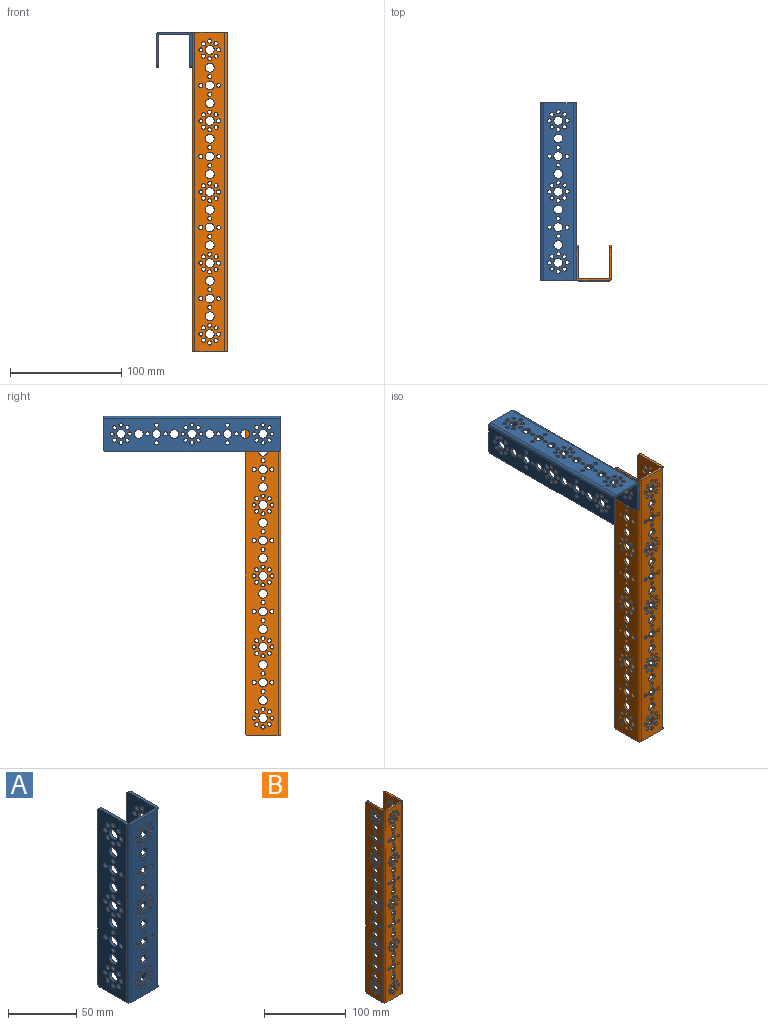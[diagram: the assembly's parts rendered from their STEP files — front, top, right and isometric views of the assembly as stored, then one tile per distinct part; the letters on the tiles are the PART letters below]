
ASSEMBLY  parts=2 mates=1
PART A: 141 faces, bbox 32x32x160 mm
  f0: cylinder r=2.5mm len=160mm, axis (0,0,-1), area 628.3mm2, adj f1,f11,f12,f13
  f1: plane 160x27mm, normal (0,-1,0), area 3523.5mm2, adj f0,f2,f12,f13,f18,f23,f24,f25
  f2: cylinder r=2.5mm len=160mm, axis (0,0,-1), area 628.3mm2, adj f1,f3,f12,f13
  f3: plane 160x29.5mm, normal (1,0,0), area 3920.9mm2, adj f2,f4,f12,f13,f14,f17,f20,f22
  f4: plane 155x2mm, normal (0,1,0), area 310mm2, adj f3,f5,f14,f17
  f5: plane 160x29.5mm, normal (-1,0,0), area 3920.9mm2, adj f4,f6,f12,f13,f14,f17,f20,f22
  f6: cylinder r=0.5mm len=160mm, axis (0,0,-1), area 125.7mm2, adj f5,f7,f12,f13
  f7: plane 160x27mm, normal (0,1,0), area 3523.5mm2, adj f6,f8,f12,f13,f18,f23,f24,f25
  f8: cylinder r=0.5mm len=160mm, axis (0,0,-1), area 125.7mm2, adj f7,f9,f12,f13
  f9: plane 160x29.5mm, normal (1,0,0), area 3920.9mm2, adj f8,f10,f12,f13,f15,f16,f19,f21
  f10: plane 155x2mm, normal (0,1,0), area 310mm2, adj f9,f11,f15,f16
  f11: plane 160x29.5mm, normal (-1,0,0), area 3920.9mm2, adj f0,f10,f12,f13,f15,f16,f19,f21
  f12: plane 32x29.5mm, normal (0,0,1), area 171.4mm2, adj f0,f1,f2,f3,f5,f6,f7,f8
  f13: plane 32x29.5mm, normal (0,0,-1), area 171.4mm2, adj f0,f1,f2,f3,f5,f6,f7,f8
  f14: cylinder r=2.5mm len=2.5mm, axis (1,0,0), area 7.9mm2, adj f3,f4,f5,f12
  f15: cylinder r=2.5mm len=2.5mm, axis (1,0,0), area 7.9mm2, adj f9,f10,f11,f12
  f16: cylinder r=2.5mm len=2.5mm, axis (-1,0,0), area 7.9mm2, adj f9,f10,f11,f13
  f17: cylinder r=2.5mm len=2.5mm, axis (-1,0,0), area 7.9mm2, adj f3,f4,f5,f13
  f18: cylinder r=4mm len=8mm, axis (0,-1,0), area 50.3mm2, adj f1,f7
  f19: cylinder r=4mm len=8mm, axis (-1,0,0), area 50.3mm2, adj f9,f11
  f20: cylinder r=4mm len=8mm, axis (-1,0,0), area 50.3mm2, adj f3,f5
  f21: cylinder r=1.85mm len=3.7mm, axis (-1,0,0), area 23.2mm2, adj f9,f11
  f22: cylinder r=1.85mm len=3.7mm, axis (-1,0,0), area 23.2mm2, adj f3,f5
  f23: cylinder r=1.85mm len=3.7mm, axis (0,-1,0), area 23.2mm2, adj f1,f7
  f24: cylinder r=4mm len=8mm, axis (0,-1,0), area 50.3mm2, adj f1,f7
  f25: cylinder r=4mm len=8mm, axis (0,-1,0), area 50.3mm2, adj f1,f7
  f26: cylinder r=4mm len=8mm, axis (0,-1,0), area 50.3mm2, adj f1,f7
  f27: cylinder r=4mm len=8mm, axis (0,-1,0), area 50.3mm2, adj f1,f7
  f28: cylinder r=4mm len=8mm, axis (0,-1,0), area 50.3mm2, adj f1,f7
  f29: cylinder r=4mm len=8mm, axis (0,-1,0), area 50.3mm2, adj f1,f7
  f30: cylinder r=4mm len=8mm, axis (0,-1,0), area 50.3mm2, adj f1,f7
  f31: cylinder r=4mm len=8mm, axis (0,-1,0), area 50.3mm2, adj f1,f7
  f32: cylinder r=4mm len=8mm, axis (-1,0,0), area 50.3mm2, adj f9,f11
  f33: cylinder r=4mm len=8mm, axis (-1,0,0), area 50.3mm2, adj f3,f5
  f34: cylinder r=4mm len=8mm, axis (-1,0,0), area 50.3mm2, adj f9,f11
  f35: cylinder r=4mm len=8mm, axis (-1,0,0), area 50.3mm2, adj f3,f5
  f36: cylinder r=4mm len=8mm, axis (-1,0,0), area 50.3mm2, adj f9,f11
  f37: cylinder r=4mm len=8mm, axis (-1,0,0), area 50.3mm2, adj f3,f5
  f38: cylinder r=4mm len=8mm, axis (-1,0,0), area 50.3mm2, adj f9,f11
  f39: cylinder r=4mm len=8mm, axis (-1,0,0), area 50.3mm2, adj f3,f5
  f40: cylinder r=4mm len=8mm, axis (-1,0,0), area 50.3mm2, adj f9,f11
  f41: cylinder r=4mm len=8mm, axis (-1,0,0), area 50.3mm2, adj f3,f5
  f42: cylinder r=4mm len=8mm, axis (-1,0,0), area 50.3mm2, adj f9,f11
  f43: cylinder r=4mm len=8mm, axis (-1,0,0), area 50.3mm2, adj f3,f5
  f44: cylinder r=4mm len=8mm, axis (-1,0,0), area 50.3mm2, adj f9,f11
  f45: cylinder r=4mm len=8mm, axis (-1,0,0), area 50.3mm2, adj f3,f5
  f46: cylinder r=4mm len=8mm, axis (-1,0,0), area 50.3mm2, adj f9,f11
  f47: cylinder r=4mm len=8mm, axis (-1,0,0), area 50.3mm2, adj f3,f5
  f48: cylinder r=1.85mm len=3.7mm, axis (0,-1,0), area 23.2mm2, adj f1,f7
  f49: cylinder r=1.85mm len=3.7mm, axis (0,-1,0), area 23.2mm2, adj f1,f7
  f50: cylinder r=1.85mm len=3.7mm, axis (0,-1,0), area 23.2mm2, adj f1,f7
  f51: cylinder r=1.85mm len=3.7mm, axis (0,-1,0), area 23.2mm2, adj f1,f7
  f52: cylinder r=1.85mm len=3.7mm, axis (0,-1,0), area 23.2mm2, adj f1,f7
  f53: cylinder r=1.85mm len=3.7mm, axis (0,-1,0), area 23.2mm2, adj f1,f7
  f54: cylinder r=1.85mm len=3.7mm, axis (0,-1,0), area 23.2mm2, adj f1,f7
  f55: cylinder r=1.85mm len=3.7mm, axis (-1,0,0), area 23.2mm2, adj f9,f11
  f56: cylinder r=1.85mm len=3.7mm, axis (-1,0,0), area 23.2mm2, adj f3,f5
  f57: cylinder r=1.85mm len=3.7mm, axis (-1,0,0), area 23.2mm2, adj f9,f11
  f58: cylinder r=1.85mm len=3.7mm, axis (-1,0,0), area 23.2mm2, adj f3,f5
  f59: cylinder r=1.85mm len=3.7mm, axis (-1,0,0), area 23.2mm2, adj f9,f11
  f60: cylinder r=1.85mm len=3.7mm, axis (-1,0,0), area 23.2mm2, adj f3,f5
  f61: cylinder r=1.85mm len=3.7mm, axis (-1,0,0), area 23.2mm2, adj f9,f11
  f62: cylinder r=1.85mm len=3.7mm, axis (-1,0,0), area 23.2mm2, adj f3,f5
  f63: cylinder r=1.85mm len=3.7mm, axis (-1,0,0), area 23.2mm2, adj f9,f11
  f64: cylinder r=1.85mm len=3.7mm, axis (-1,0,0), area 23.2mm2, adj f3,f5
  f65: cylinder r=1.85mm len=3.7mm, axis (-1,0,0), area 23.2mm2, adj f9,f11
  f66: cylinder r=1.85mm len=3.7mm, axis (-1,0,0), area 23.2mm2, adj f3,f5
  f67: cylinder r=1.85mm len=3.7mm, axis (-1,0,0), area 23.2mm2, adj f9,f11
  f68: cylinder r=1.85mm len=3.7mm, axis (-1,0,0), area 23.2mm2, adj f3,f5
  f69: cylinder r=1.85mm len=3.7mm, axis (0,-1,0), area 23.2mm2, adj f1,f7
  f70: cylinder r=1.85mm len=3.7mm, axis (-1,0,0), area 23.2mm2, adj f9,f11
  f71: cylinder r=1.85mm len=3.7mm, axis (-1,0,0), area 23.2mm2, adj f3,f5
  f72: cylinder r=1.85mm len=3.7mm, axis (0,-1,0), area 23.2mm2, adj f1,f7
  f73: cylinder r=1.85mm len=3.7mm, axis (0,-1,0), area 23.2mm2, adj f1,f7
  f74: cylinder r=1.85mm len=3.7mm, axis (0,-1,0), area 23.2mm2, adj f1,f7
  f75: cylinder r=1.85mm len=3.7mm, axis (-1,0,0), area 23.2mm2, adj f9,f11
  f76: cylinder r=1.85mm len=3.7mm, axis (-1,0,0), area 23.2mm2, adj f3,f5
  f77: cylinder r=1.85mm len=3.7mm, axis (-1,0,0), area 23.2mm2, adj f9,f11
  f78: cylinder r=1.85mm len=3.7mm, axis (-1,0,0), area 23.2mm2, adj f3,f5
  f79: cylinder r=1.85mm len=3.7mm, axis (-1,0,0), area 23.2mm2, adj f9,f11
  f80: cylinder r=1.85mm len=3.7mm, axis (-1,0,0), area 23.2mm2, adj f3,f5
  f81: cylinder r=1.85mm len=3.7mm, axis (0,-1,0), area 23.2mm2, adj f1,f7
  f82: cylinder r=1.85mm len=3.7mm, axis (0,-1,0), area 23.2mm2, adj f1,f7
  f83: cylinder r=1.85mm len=3.7mm, axis (0,-1,0), area 23.2mm2, adj f1,f7
  f84: cylinder r=1.85mm len=3.7mm, axis (0,-1,0), area 23.2mm2, adj f1,f7
  f85: cylinder r=1.85mm len=3.7mm, axis (0,-1,0), area 23.2mm2, adj f1,f7
  f86: cylinder r=1.85mm len=3.7mm, axis (0,-1,0), area 23.2mm2, adj f1,f7
  f87: cylinder r=1.85mm len=3.7mm, axis (0,-1,0), area 23.2mm2, adj f1,f7
  f88: cylinder r=1.85mm len=3.7mm, axis (0,-1,0), area 23.2mm2, adj f1,f7
  f89: cylinder r=1.85mm len=3.7mm, axis (-1,0,0), area 23.2mm2, adj f9,f11
  f90: cylinder r=1.85mm len=3.7mm, axis (-1,0,0), area 23.2mm2, adj f3,f5
  f91: cylinder r=1.85mm len=3.7mm, axis (-1,0,0), area 23.2mm2, adj f9,f11
  f92: cylinder r=1.85mm len=3.7mm, axis (-1,0,0), area 23.2mm2, adj f3,f5
  f93: cylinder r=1.85mm len=3.7mm, axis (-1,0,0), area 23.2mm2, adj f9,f11
  f94: cylinder r=1.85mm len=3.7mm, axis (-1,0,0), area 23.2mm2, adj f3,f5
  f95: cylinder r=1.85mm len=3.7mm, axis (-1,0,0), area 23.2mm2, adj f9,f11
  f96: cylinder r=1.85mm len=3.7mm, axis (-1,0,0), area 23.2mm2, adj f3,f5
  f97: cylinder r=1.85mm len=3.7mm, axis (-1,0,0), area 23.2mm2, adj f9,f11
  f98: cylinder r=1.85mm len=3.7mm, axis (-1,0,0), area 23.2mm2, adj f3,f5
  f99: cylinder r=1.85mm len=3.7mm, axis (-1,0,0), area 23.2mm2, adj f9,f11
  f100: cylinder r=1.85mm len=3.7mm, axis (-1,0,0), area 23.2mm2, adj f3,f5
  f101: cylinder r=1.85mm len=3.7mm, axis (-1,0,0), area 23.2mm2, adj f9,f11
  f102: cylinder r=1.85mm len=3.7mm, axis (-1,0,0), area 23.2mm2, adj f3,f5
  f103: cylinder r=1.85mm len=3.7mm, axis (-1,0,0), area 23.2mm2, adj f9,f11
  f104: cylinder r=1.85mm len=3.7mm, axis (-1,0,0), area 23.2mm2, adj f3,f5
  f105: cylinder r=1.85mm len=3.7mm, axis (0,-1,0), area 23.2mm2, adj f1,f7
  f106: cylinder r=1.85mm len=3.7mm, axis (0,-1,0), area 23.2mm2, adj f1,f7
  f107: cylinder r=1.85mm len=3.7mm, axis (0,-1,0), area 23.2mm2, adj f1,f7
  f108: cylinder r=1.85mm len=3.7mm, axis (0,-1,0), area 23.2mm2, adj f1,f7
  f109: cylinder r=1.85mm len=3.7mm, axis (-1,0,0), area 23.2mm2, adj f3,f5
  f110: cylinder r=1.85mm len=3.7mm, axis (-1,0,0), area 23.2mm2, adj f3,f5
  f111: cylinder r=1.85mm len=3.7mm, axis (-1,0,0), area 23.2mm2, adj f3,f5
  f112: cylinder r=1.85mm len=3.7mm, axis (-1,0,0), area 23.2mm2, adj f3,f5
  f113: cylinder r=1.85mm len=3.7mm, axis (-1,0,0), area 23.2mm2, adj f9,f11
  f114: cylinder r=1.85mm len=3.7mm, axis (-1,0,0), area 23.2mm2, adj f9,f11
  f115: cylinder r=1.85mm len=3.7mm, axis (-1,0,0), area 23.2mm2, adj f9,f11
  f116: cylinder r=1.85mm len=3.7mm, axis (-1,0,0), area 23.2mm2, adj f9,f11
  f117: cylinder r=1.85mm len=3.7mm, axis (-1,0,0), area 23.2mm2, adj f3,f5
  f118: cylinder r=1.85mm len=3.7mm, axis (-1,0,0), area 23.2mm2, adj f3,f5
  f119: cylinder r=1.85mm len=3.7mm, axis (-1,0,0), area 23.2mm2, adj f3,f5
  f120: cylinder r=1.85mm len=3.7mm, axis (-1,0,0), area 23.2mm2, adj f3,f5
  f121: cylinder r=1.85mm len=3.7mm, axis (-1,0,0), area 23.2mm2, adj f3,f5
  f122: cylinder r=1.85mm len=3.7mm, axis (-1,0,0), area 23.2mm2, adj f3,f5
  f123: cylinder r=1.85mm len=3.7mm, axis (-1,0,0), area 23.2mm2, adj f3,f5
  f124: cylinder r=1.85mm len=3.7mm, axis (-1,0,0), area 23.2mm2, adj f3,f5
  f125: cylinder r=1.85mm len=3.7mm, axis (-1,0,0), area 23.2mm2, adj f9,f11
  f126: cylinder r=1.85mm len=3.7mm, axis (-1,0,0), area 23.2mm2, adj f9,f11
  f127: cylinder r=1.85mm len=3.7mm, axis (-1,0,0), area 23.2mm2, adj f9,f11
  f128: cylinder r=1.85mm len=3.7mm, axis (-1,0,0), area 23.2mm2, adj f9,f11
  f129: cylinder r=1.85mm len=3.7mm, axis (-1,0,0), area 23.2mm2, adj f9,f11
  f130: cylinder r=1.85mm len=3.7mm, axis (-1,0,0), area 23.2mm2, adj f9,f11
  f131: cylinder r=1.85mm len=3.7mm, axis (-1,0,0), area 23.2mm2, adj f9,f11
  f132: cylinder r=1.85mm len=3.7mm, axis (-1,0,0), area 23.2mm2, adj f9,f11
  f133: cylinder r=1.85mm len=3.7mm, axis (0,-1,0), area 23.2mm2, adj f1,f7
  f134: cylinder r=1.85mm len=3.7mm, axis (0,-1,0), area 23.2mm2, adj f1,f7
  f135: cylinder r=1.85mm len=3.7mm, axis (0,-1,0), area 23.2mm2, adj f1,f7
  f136: cylinder r=1.85mm len=3.7mm, axis (0,-1,0), area 23.2mm2, adj f1,f7
  f137: cylinder r=1.85mm len=3.7mm, axis (0,-1,0), area 23.2mm2, adj f1,f7
  f138: cylinder r=1.85mm len=3.7mm, axis (0,-1,0), area 23.2mm2, adj f1,f7
  f139: cylinder r=1.85mm len=3.7mm, axis (0,-1,0), area 23.2mm2, adj f1,f7
  f140: cylinder r=1.85mm len=3.7mm, axis (0,-1,0), area 23.2mm2, adj f1,f7
PART B: 237 faces, bbox 32x32x288 mm
  f0: plane 288x29.5mm, normal (1,0,0), area 7036.7mm2, adj f7,f8,f12,f13,f14,f17,f20,f22
  f1: plane 288x29.5mm, normal (-1,0,0), area 7036.7mm2, adj f8,f9,f12,f13,f14,f17,f20,f22
  f2: plane 288x29.5mm, normal (1,0,0), area 7036.7mm2, adj f10,f11,f12,f13,f15,f16,f19,f21
  f3: plane 288x29.5mm, normal (-1,0,0), area 7036.7mm2, adj f6,f11,f12,f13,f15,f16,f19,f21
  f4: plane 288x27mm, normal (0,-1,0), area 6319.4mm2, adj f6,f7,f12,f13,f18,f23,f24,f25
  f5: plane 288x27mm, normal (0,1,0), area 6319.4mm2, adj f9,f10,f12,f13,f18,f23,f24,f25
  f6: cylinder r=2.5mm len=288mm, axis (0,0,-1), area 1131mm2, adj f3,f4,f12,f13
  f7: cylinder r=2.5mm len=288mm, axis (0,0,-1), area 1131mm2, adj f0,f4,f12,f13
  f8: plane 283x2mm, normal (0,1,0), area 566mm2, adj f0,f1,f14,f17
  f9: cylinder r=0.5mm len=288mm, axis (0,0,-1), area 226.2mm2, adj f1,f5,f12,f13
  f10: cylinder r=0.5mm len=288mm, axis (0,0,-1), area 226.2mm2, adj f2,f5,f12,f13
  f11: plane 283x2mm, normal (0,1,0), area 566mm2, adj f2,f3,f15,f16
  f12: plane 32x29.5mm, normal (0,0,1), area 171.4mm2, adj f0,f1,f2,f3,f4,f5,f6,f7
  f13: plane 32x29.5mm, normal (0,0,-1), area 171.4mm2, adj f0,f1,f2,f3,f4,f5,f6,f7
  f14: cylinder r=2.5mm len=2.5mm, axis (1,0,0), area 7.9mm2, adj f0,f1,f8,f12
  f15: cylinder r=2.5mm len=2.5mm, axis (1,0,0), area 7.9mm2, adj f2,f3,f11,f12
  f16: cylinder r=2.5mm len=2.5mm, axis (-1,0,0), area 7.9mm2, adj f2,f3,f11,f13
  f17: cylinder r=2.5mm len=2.5mm, axis (-1,0,0), area 7.9mm2, adj f0,f1,f8,f13
  f18: cylinder r=4mm len=8mm, axis (0,-1,0), area 50.3mm2, adj f4,f5
  f19: cylinder r=4mm len=8mm, axis (-1,0,0), area 50.3mm2, adj f2,f3
  f20: cylinder r=4mm len=8mm, axis (-1,0,0), area 50.3mm2, adj f0,f1
  f21: cylinder r=1.85mm len=3.7mm, axis (-1,0,0), area 23.2mm2, adj f2,f3
  f22: cylinder r=1.85mm len=3.7mm, axis (-1,0,0), area 23.2mm2, adj f0,f1
  f23: cylinder r=1.85mm len=3.7mm, axis (0,-1,0), area 23.2mm2, adj f4,f5
  f24: cylinder r=4mm len=8mm, axis (0,-1,0), area 50.3mm2, adj f4,f5
  f25: cylinder r=4mm len=8mm, axis (0,-1,0), area 50.3mm2, adj f4,f5
  f26: cylinder r=4mm len=8mm, axis (0,-1,0), area 50.3mm2, adj f4,f5
  f27: cylinder r=4mm len=8mm, axis (0,-1,0), area 50.3mm2, adj f4,f5
  f28: cylinder r=4mm len=8mm, axis (0,-1,0), area 50.3mm2, adj f4,f5
  f29: cylinder r=4mm len=8mm, axis (0,-1,0), area 50.3mm2, adj f4,f5
  f30: cylinder r=4mm len=8mm, axis (0,-1,0), area 50.3mm2, adj f4,f5
  f31: cylinder r=4mm len=8mm, axis (0,-1,0), area 50.3mm2, adj f4,f5
  f32: cylinder r=4mm len=8mm, axis (0,-1,0), area 50.3mm2, adj f4,f5
  f33: cylinder r=4mm len=8mm, axis (0,-1,0), area 50.3mm2, adj f4,f5
  f34: cylinder r=4mm len=8mm, axis (0,-1,0), area 50.3mm2, adj f4,f5
  f35: cylinder r=4mm len=8mm, axis (0,-1,0), area 50.3mm2, adj f4,f5
  f36: cylinder r=4mm len=8mm, axis (0,-1,0), area 50.3mm2, adj f4,f5
  f37: cylinder r=4mm len=8mm, axis (0,-1,0), area 50.3mm2, adj f4,f5
  f38: cylinder r=4mm len=8mm, axis (0,-1,0), area 50.3mm2, adj f4,f5
  f39: cylinder r=4mm len=8mm, axis (0,-1,0), area 50.3mm2, adj f4,f5
  f40: cylinder r=4mm len=8mm, axis (-1,0,0), area 50.3mm2, adj f2,f3
  f41: cylinder r=4mm len=8mm, axis (-1,0,0), area 50.3mm2, adj f0,f1
  f42: cylinder r=4mm len=8mm, axis (-1,0,0), area 50.3mm2, adj f2,f3
  f43: cylinder r=4mm len=8mm, axis (-1,0,0), area 50.3mm2, adj f0,f1
  f44: cylinder r=4mm len=8mm, axis (-1,0,0), area 50.3mm2, adj f2,f3
  f45: cylinder r=4mm len=8mm, axis (-1,0,0), area 50.3mm2, adj f0,f1
  f46: cylinder r=4mm len=8mm, axis (-1,0,0), area 50.3mm2, adj f2,f3
  f47: cylinder r=4mm len=8mm, axis (-1,0,0), area 50.3mm2, adj f0,f1
  f48: cylinder r=4mm len=8mm, axis (-1,0,0), area 50.3mm2, adj f2,f3
  f49: cylinder r=4mm len=8mm, axis (-1,0,0), area 50.3mm2, adj f0,f1
  f50: cylinder r=4mm len=8mm, axis (-1,0,0), area 50.3mm2, adj f2,f3
  f51: cylinder r=4mm len=8mm, axis (-1,0,0), area 50.3mm2, adj f0,f1
  f52: cylinder r=4mm len=8mm, axis (-1,0,0), area 50.3mm2, adj f2,f3
  f53: cylinder r=4mm len=8mm, axis (-1,0,0), area 50.3mm2, adj f0,f1
  f54: cylinder r=4mm len=8mm, axis (-1,0,0), area 50.3mm2, adj f2,f3
  f55: cylinder r=4mm len=8mm, axis (-1,0,0), area 50.3mm2, adj f0,f1
  f56: cylinder r=4mm len=8mm, axis (-1,0,0), area 50.3mm2, adj f2,f3
  f57: cylinder r=4mm len=8mm, axis (-1,0,0), area 50.3mm2, adj f0,f1
  f58: cylinder r=4mm len=8mm, axis (-1,0,0), area 50.3mm2, adj f2,f3
  f59: cylinder r=4mm len=8mm, axis (-1,0,0), area 50.3mm2, adj f0,f1
  f60: cylinder r=4mm len=8mm, axis (-1,0,0), area 50.3mm2, adj f2,f3
  f61: cylinder r=4mm len=8mm, axis (-1,0,0), area 50.3mm2, adj f0,f1
  f62: cylinder r=4mm len=8mm, axis (-1,0,0), area 50.3mm2, adj f2,f3
  f63: cylinder r=4mm len=8mm, axis (-1,0,0), area 50.3mm2, adj f0,f1
  f64: cylinder r=4mm len=8mm, axis (-1,0,0), area 50.3mm2, adj f2,f3
  f65: cylinder r=4mm len=8mm, axis (-1,0,0), area 50.3mm2, adj f0,f1
  f66: cylinder r=4mm len=8mm, axis (-1,0,0), area 50.3mm2, adj f2,f3
  f67: cylinder r=4mm len=8mm, axis (-1,0,0), area 50.3mm2, adj f0,f1
  f68: cylinder r=4mm len=8mm, axis (-1,0,0), area 50.3mm2, adj f2,f3
  f69: cylinder r=4mm len=8mm, axis (-1,0,0), area 50.3mm2, adj f0,f1
  f70: cylinder r=4mm len=8mm, axis (-1,0,0), area 50.3mm2, adj f2,f3
  f71: cylinder r=4mm len=8mm, axis (-1,0,0), area 50.3mm2, adj f0,f1
  f72: cylinder r=1.85mm len=3.7mm, axis (0,-1,0), area 23.2mm2, adj f4,f5
  f73: cylinder r=1.85mm len=3.7mm, axis (0,-1,0), area 23.2mm2, adj f4,f5
  f74: cylinder r=1.85mm len=3.7mm, axis (0,-1,0), area 23.2mm2, adj f4,f5
  f75: cylinder r=1.85mm len=3.7mm, axis (0,-1,0), area 23.2mm2, adj f4,f5
  f76: cylinder r=1.85mm len=3.7mm, axis (0,-1,0), area 23.2mm2, adj f4,f5
  f77: cylinder r=1.85mm len=3.7mm, axis (0,-1,0), area 23.2mm2, adj f4,f5
  f78: cylinder r=1.85mm len=3.7mm, axis (0,-1,0), area 23.2mm2, adj f4,f5
  f79: cylinder r=1.85mm len=3.7mm, axis (-1,0,0), area 23.2mm2, adj f2,f3
  f80: cylinder r=1.85mm len=3.7mm, axis (-1,0,0), area 23.2mm2, adj f0,f1
  f81: cylinder r=1.85mm len=3.7mm, axis (-1,0,0), area 23.2mm2, adj f2,f3
  f82: cylinder r=1.85mm len=3.7mm, axis (-1,0,0), area 23.2mm2, adj f0,f1
  f83: cylinder r=1.85mm len=3.7mm, axis (-1,0,0), area 23.2mm2, adj f2,f3
  f84: cylinder r=1.85mm len=3.7mm, axis (-1,0,0), area 23.2mm2, adj f0,f1
  f85: cylinder r=1.85mm len=3.7mm, axis (-1,0,0), area 23.2mm2, adj f2,f3
  f86: cylinder r=1.85mm len=3.7mm, axis (-1,0,0), area 23.2mm2, adj f0,f1
  f87: cylinder r=1.85mm len=3.7mm, axis (-1,0,0), area 23.2mm2, adj f2,f3
  f88: cylinder r=1.85mm len=3.7mm, axis (-1,0,0), area 23.2mm2, adj f0,f1
  f89: cylinder r=1.85mm len=3.7mm, axis (-1,0,0), area 23.2mm2, adj f2,f3
  f90: cylinder r=1.85mm len=3.7mm, axis (-1,0,0), area 23.2mm2, adj f0,f1
  f91: cylinder r=1.85mm len=3.7mm, axis (-1,0,0), area 23.2mm2, adj f2,f3
  f92: cylinder r=1.85mm len=3.7mm, axis (-1,0,0), area 23.2mm2, adj f0,f1
  f93: cylinder r=1.85mm len=3.7mm, axis (0,-1,0), area 23.2mm2, adj f4,f5
  f94: cylinder r=1.85mm len=3.7mm, axis (-1,0,0), area 23.2mm2, adj f2,f3
  f95: cylinder r=1.85mm len=3.7mm, axis (-1,0,0), area 23.2mm2, adj f0,f1
  f96: cylinder r=1.85mm len=3.7mm, axis (0,-1,0), area 23.2mm2, adj f4,f5
  f97: cylinder r=1.85mm len=3.7mm, axis (0,-1,0), area 23.2mm2, adj f4,f5
  f98: cylinder r=1.85mm len=3.7mm, axis (0,-1,0), area 23.2mm2, adj f4,f5
  f99: cylinder r=1.85mm len=3.7mm, axis (-1,0,0), area 23.2mm2, adj f2,f3
  f100: cylinder r=1.85mm len=3.7mm, axis (-1,0,0), area 23.2mm2, adj f0,f1
  f101: cylinder r=1.85mm len=3.7mm, axis (-1,0,0), area 23.2mm2, adj f2,f3
  f102: cylinder r=1.85mm len=3.7mm, axis (-1,0,0), area 23.2mm2, adj f0,f1
  f103: cylinder r=1.85mm len=3.7mm, axis (-1,0,0), area 23.2mm2, adj f2,f3
  f104: cylinder r=1.85mm len=3.7mm, axis (-1,0,0), area 23.2mm2, adj f0,f1
  f105: cylinder r=1.85mm len=3.7mm, axis (0,-1,0), area 23.2mm2, adj f4,f5
  f106: cylinder r=1.85mm len=3.7mm, axis (0,-1,0), area 23.2mm2, adj f4,f5
  f107: cylinder r=1.85mm len=3.7mm, axis (0,-1,0), area 23.2mm2, adj f4,f5
  f108: cylinder r=1.85mm len=3.7mm, axis (0,-1,0), area 23.2mm2, adj f4,f5
  f109: cylinder r=1.85mm len=3.7mm, axis (0,-1,0), area 23.2mm2, adj f4,f5
  f110: cylinder r=1.85mm len=3.7mm, axis (0,-1,0), area 23.2mm2, adj f4,f5
  f111: cylinder r=1.85mm len=3.7mm, axis (0,-1,0), area 23.2mm2, adj f4,f5
  f112: cylinder r=1.85mm len=3.7mm, axis (0,-1,0), area 23.2mm2, adj f4,f5
  f113: cylinder r=1.85mm len=3.7mm, axis (0,-1,0), area 23.2mm2, adj f4,f5
  f114: cylinder r=1.85mm len=3.7mm, axis (0,-1,0), area 23.2mm2, adj f4,f5
  f115: cylinder r=1.85mm len=3.7mm, axis (0,-1,0), area 23.2mm2, adj f4,f5
  f116: cylinder r=1.85mm len=3.7mm, axis (0,-1,0), area 23.2mm2, adj f4,f5
  f117: cylinder r=1.85mm len=3.7mm, axis (0,-1,0), area 23.2mm2, adj f4,f5
  f118: cylinder r=1.85mm len=3.7mm, axis (0,-1,0), area 23.2mm2, adj f4,f5
  f119: cylinder r=1.85mm len=3.7mm, axis (0,-1,0), area 23.2mm2, adj f4,f5
  f120: cylinder r=1.85mm len=3.7mm, axis (0,-1,0), area 23.2mm2, adj f4,f5
  f121: cylinder r=1.85mm len=3.7mm, axis (-1,0,0), area 23.2mm2, adj f2,f3
  f122: cylinder r=1.85mm len=3.7mm, axis (-1,0,0), area 23.2mm2, adj f0,f1
  f123: cylinder r=1.85mm len=3.7mm, axis (-1,0,0), area 23.2mm2, adj f2,f3
  f124: cylinder r=1.85mm len=3.7mm, axis (-1,0,0), area 23.2mm2, adj f0,f1
  f125: cylinder r=1.85mm len=3.7mm, axis (-1,0,0), area 23.2mm2, adj f2,f3
  f126: cylinder r=1.85mm len=3.7mm, axis (-1,0,0), area 23.2mm2, adj f0,f1
  f127: cylinder r=1.85mm len=3.7mm, axis (-1,0,0), area 23.2mm2, adj f2,f3
  f128: cylinder r=1.85mm len=3.7mm, axis (-1,0,0), area 23.2mm2, adj f0,f1
  f129: cylinder r=1.85mm len=3.7mm, axis (-1,0,0), area 23.2mm2, adj f2,f3
  f130: cylinder r=1.85mm len=3.7mm, axis (-1,0,0), area 23.2mm2, adj f0,f1
  f131: cylinder r=1.85mm len=3.7mm, axis (-1,0,0), area 23.2mm2, adj f2,f3
  f132: cylinder r=1.85mm len=3.7mm, axis (-1,0,0), area 23.2mm2, adj f0,f1
  f133: cylinder r=1.85mm len=3.7mm, axis (-1,0,0), area 23.2mm2, adj f2,f3
  f134: cylinder r=1.85mm len=3.7mm, axis (-1,0,0), area 23.2mm2, adj f0,f1
  f135: cylinder r=1.85mm len=3.7mm, axis (-1,0,0), area 23.2mm2, adj f2,f3
  f136: cylinder r=1.85mm len=3.7mm, axis (-1,0,0), area 23.2mm2, adj f0,f1
  f137: cylinder r=1.85mm len=3.7mm, axis (-1,0,0), area 23.2mm2, adj f2,f3
  f138: cylinder r=1.85mm len=3.7mm, axis (-1,0,0), area 23.2mm2, adj f0,f1
  f139: cylinder r=1.85mm len=3.7mm, axis (-1,0,0), area 23.2mm2, adj f2,f3
  f140: cylinder r=1.85mm len=3.7mm, axis (-1,0,0), area 23.2mm2, adj f0,f1
  f141: cylinder r=1.85mm len=3.7mm, axis (-1,0,0), area 23.2mm2, adj f2,f3
  f142: cylinder r=1.85mm len=3.7mm, axis (-1,0,0), area 23.2mm2, adj f0,f1
  f143: cylinder r=1.85mm len=3.7mm, axis (-1,0,0), area 23.2mm2, adj f2,f3
  f144: cylinder r=1.85mm len=3.7mm, axis (-1,0,0), area 23.2mm2, adj f0,f1
  f145: cylinder r=1.85mm len=3.7mm, axis (-1,0,0), area 23.2mm2, adj f2,f3
  f146: cylinder r=1.85mm len=3.7mm, axis (-1,0,0), area 23.2mm2, adj f0,f1
  f147: cylinder r=1.85mm len=3.7mm, axis (-1,0,0), area 23.2mm2, adj f2,f3
  f148: cylinder r=1.85mm len=3.7mm, axis (-1,0,0), area 23.2mm2, adj f0,f1
  f149: cylinder r=1.85mm len=3.7mm, axis (-1,0,0), area 23.2mm2, adj f2,f3
  f150: cylinder r=1.85mm len=3.7mm, axis (-1,0,0), area 23.2mm2, adj f0,f1
  f151: cylinder r=1.85mm len=3.7mm, axis (-1,0,0), area 23.2mm2, adj f2,f3
  f152: cylinder r=1.85mm len=3.7mm, axis (-1,0,0), area 23.2mm2, adj f0,f1
  f153: cylinder r=1.85mm len=3.7mm, axis (0,-1,0), area 23.2mm2, adj f4,f5
  f154: cylinder r=1.85mm len=3.7mm, axis (0,-1,0), area 23.2mm2, adj f4,f5
  f155: cylinder r=1.85mm len=3.7mm, axis (0,-1,0), area 23.2mm2, adj f4,f5
  f156: cylinder r=1.85mm len=3.7mm, axis (0,-1,0), area 23.2mm2, adj f4,f5
  f157: cylinder r=1.85mm len=3.7mm, axis (-1,0,0), area 23.2mm2, adj f2,f3
  f158: cylinder r=1.85mm len=3.7mm, axis (-1,0,0), area 23.2mm2, adj f0,f1
  f159: cylinder r=1.85mm len=3.7mm, axis (-1,0,0), area 23.2mm2, adj f2,f3
  f160: cylinder r=1.85mm len=3.7mm, axis (-1,0,0), area 23.2mm2, adj f0,f1
  f161: cylinder r=1.85mm len=3.7mm, axis (-1,0,0), area 23.2mm2, adj f2,f3
  f162: cylinder r=1.85mm len=3.7mm, axis (-1,0,0), area 23.2mm2, adj f0,f1
  f163: cylinder r=1.85mm len=3.7mm, axis (-1,0,0), area 23.2mm2, adj f2,f3
  f164: cylinder r=1.85mm len=3.7mm, axis (-1,0,0), area 23.2mm2, adj f0,f1
  f165: cylinder r=1.85mm len=3.7mm, axis (0,-1,0), area 23.2mm2, adj f4,f5
  f166: cylinder r=1.85mm len=3.7mm, axis (0,-1,0), area 23.2mm2, adj f4,f5
  f167: cylinder r=1.85mm len=3.7mm, axis (0,-1,0), area 23.2mm2, adj f4,f5
  f168: cylinder r=1.85mm len=3.7mm, axis (0,-1,0), area 23.2mm2, adj f4,f5
  f169: cylinder r=1.85mm len=3.7mm, axis (0,-1,0), area 23.2mm2, adj f4,f5
  f170: cylinder r=1.85mm len=3.7mm, axis (0,-1,0), area 23.2mm2, adj f4,f5
  f171: cylinder r=1.85mm len=3.7mm, axis (0,-1,0), area 23.2mm2, adj f4,f5
  f172: cylinder r=1.85mm len=3.7mm, axis (0,-1,0), area 23.2mm2, adj f4,f5
  f173: cylinder r=1.85mm len=3.7mm, axis (0,-1,0), area 23.2mm2, adj f4,f5
  f174: cylinder r=1.85mm len=3.7mm, axis (0,-1,0), area 23.2mm2, adj f4,f5
  f175: cylinder r=1.85mm len=3.7mm, axis (0,-1,0), area 23.2mm2, adj f4,f5
  f176: cylinder r=1.85mm len=3.7mm, axis (0,-1,0), area 23.2mm2, adj f4,f5
  f177: cylinder r=1.85mm len=3.7mm, axis (0,-1,0), area 23.2mm2, adj f4,f5
  f178: cylinder r=1.85mm len=3.7mm, axis (0,-1,0), area 23.2mm2, adj f4,f5
  f179: cylinder r=1.85mm len=3.7mm, axis (0,-1,0), area 23.2mm2, adj f4,f5
  f180: cylinder r=1.85mm len=3.7mm, axis (0,-1,0), area 23.2mm2, adj f4,f5
  f181: cylinder r=1.85mm len=3.7mm, axis (-1,0,0), area 23.2mm2, adj f2,f3
  f182: cylinder r=1.85mm len=3.7mm, axis (-1,0,0), area 23.2mm2, adj f0,f1
  f183: cylinder r=1.85mm len=3.7mm, axis (-1,0,0), area 23.2mm2, adj f2,f3
  f184: cylinder r=1.85mm len=3.7mm, axis (-1,0,0), area 23.2mm2, adj f0,f1
  f185: cylinder r=1.85mm len=3.7mm, axis (-1,0,0), area 23.2mm2, adj f2,f3
  f186: cylinder r=1.85mm len=3.7mm, axis (-1,0,0), area 23.2mm2, adj f0,f1
  f187: cylinder r=1.85mm len=3.7mm, axis (-1,0,0), area 23.2mm2, adj f2,f3
  f188: cylinder r=1.85mm len=3.7mm, axis (-1,0,0), area 23.2mm2, adj f0,f1
  f189: cylinder r=1.85mm len=3.7mm, axis (-1,0,0), area 23.2mm2, adj f2,f3
  f190: cylinder r=1.85mm len=3.7mm, axis (-1,0,0), area 23.2mm2, adj f0,f1
  f191: cylinder r=1.85mm len=3.7mm, axis (-1,0,0), area 23.2mm2, adj f2,f3
  f192: cylinder r=1.85mm len=3.7mm, axis (-1,0,0), area 23.2mm2, adj f0,f1
  f193: cylinder r=1.85mm len=3.7mm, axis (-1,0,0), area 23.2mm2, adj f2,f3
  f194: cylinder r=1.85mm len=3.7mm, axis (-1,0,0), area 23.2mm2, adj f0,f1
  f195: cylinder r=1.85mm len=3.7mm, axis (-1,0,0), area 23.2mm2, adj f2,f3
  f196: cylinder r=1.85mm len=3.7mm, axis (-1,0,0), area 23.2mm2, adj f0,f1
  f197: cylinder r=1.85mm len=3.7mm, axis (-1,0,0), area 23.2mm2, adj f2,f3
  f198: cylinder r=1.85mm len=3.7mm, axis (-1,0,0), area 23.2mm2, adj f0,f1
  f199: cylinder r=1.85mm len=3.7mm, axis (-1,0,0), area 23.2mm2, adj f2,f3
  f200: cylinder r=1.85mm len=3.7mm, axis (-1,0,0), area 23.2mm2, adj f0,f1
  f201: cylinder r=1.85mm len=3.7mm, axis (-1,0,0), area 23.2mm2, adj f2,f3
  f202: cylinder r=1.85mm len=3.7mm, axis (-1,0,0), area 23.2mm2, adj f0,f1
  f203: cylinder r=1.85mm len=3.7mm, axis (-1,0,0), area 23.2mm2, adj f2,f3
  f204: cylinder r=1.85mm len=3.7mm, axis (-1,0,0), area 23.2mm2, adj f0,f1
  f205: cylinder r=1.85mm len=3.7mm, axis (-1,0,0), area 23.2mm2, adj f2,f3
  f206: cylinder r=1.85mm len=3.7mm, axis (-1,0,0), area 23.2mm2, adj f0,f1
  f207: cylinder r=1.85mm len=3.7mm, axis (-1,0,0), area 23.2mm2, adj f2,f3
  f208: cylinder r=1.85mm len=3.7mm, axis (-1,0,0), area 23.2mm2, adj f0,f1
  f209: cylinder r=1.85mm len=3.7mm, axis (-1,0,0), area 23.2mm2, adj f2,f3
  f210: cylinder r=1.85mm len=3.7mm, axis (-1,0,0), area 23.2mm2, adj f0,f1
  f211: cylinder r=1.85mm len=3.7mm, axis (-1,0,0), area 23.2mm2, adj f2,f3
  f212: cylinder r=1.85mm len=3.7mm, axis (-1,0,0), area 23.2mm2, adj f0,f1
  f213: cylinder r=1.85mm len=3.7mm, axis (0,-1,0), area 23.2mm2, adj f4,f5
  f214: cylinder r=1.85mm len=3.7mm, axis (0,-1,0), area 23.2mm2, adj f4,f5
  f215: cylinder r=1.85mm len=3.7mm, axis (0,-1,0), area 23.2mm2, adj f4,f5
  f216: cylinder r=1.85mm len=3.7mm, axis (0,-1,0), area 23.2mm2, adj f4,f5
  f217: cylinder r=1.85mm len=3.7mm, axis (0,-1,0), area 23.2mm2, adj f4,f5
  f218: cylinder r=1.85mm len=3.7mm, axis (0,-1,0), area 23.2mm2, adj f4,f5
  f219: cylinder r=1.85mm len=3.7mm, axis (0,-1,0), area 23.2mm2, adj f4,f5
  f220: cylinder r=1.85mm len=3.7mm, axis (0,-1,0), area 23.2mm2, adj f4,f5
  f221: cylinder r=1.85mm len=3.7mm, axis (-1,0,0), area 23.2mm2, adj f2,f3
  f222: cylinder r=1.85mm len=3.7mm, axis (-1,0,0), area 23.2mm2, adj f0,f1
  f223: cylinder r=1.85mm len=3.7mm, axis (-1,0,0), area 23.2mm2, adj f2,f3
  f224: cylinder r=1.85mm len=3.7mm, axis (-1,0,0), area 23.2mm2, adj f0,f1
  f225: cylinder r=1.85mm len=3.7mm, axis (-1,0,0), area 23.2mm2, adj f2,f3
  f226: cylinder r=1.85mm len=3.7mm, axis (-1,0,0), area 23.2mm2, adj f0,f1
  f227: cylinder r=1.85mm len=3.7mm, axis (-1,0,0), area 23.2mm2, adj f2,f3
  f228: cylinder r=1.85mm len=3.7mm, axis (-1,0,0), area 23.2mm2, adj f0,f1
  f229: cylinder r=1.85mm len=3.7mm, axis (-1,0,0), area 23.2mm2, adj f2,f3
  f230: cylinder r=1.85mm len=3.7mm, axis (-1,0,0), area 23.2mm2, adj f0,f1
  f231: cylinder r=1.85mm len=3.7mm, axis (-1,0,0), area 23.2mm2, adj f2,f3
  f232: cylinder r=1.85mm len=3.7mm, axis (-1,0,0), area 23.2mm2, adj f0,f1
  f233: cylinder r=1.85mm len=3.7mm, axis (-1,0,0), area 23.2mm2, adj f2,f3
  f234: cylinder r=1.85mm len=3.7mm, axis (-1,0,0), area 23.2mm2, adj f0,f1
  f235: cylinder r=1.85mm len=3.7mm, axis (-1,0,0), area 23.2mm2, adj f2,f3
  f236: cylinder r=1.85mm len=3.7mm, axis (-1,0,0), area 23.2mm2, adj f0,f1
PLACE A rot(axis=(0,0.71,-0.71),180deg) t=(-14.54,75.07,145.49)mm
PLACE B t=(17.46,-4.93,1.49)mm fixed
MATE revolute B.f54 <-> A.f38  axis (-1,0,0) through (1.46,11.07,129.49)mm
